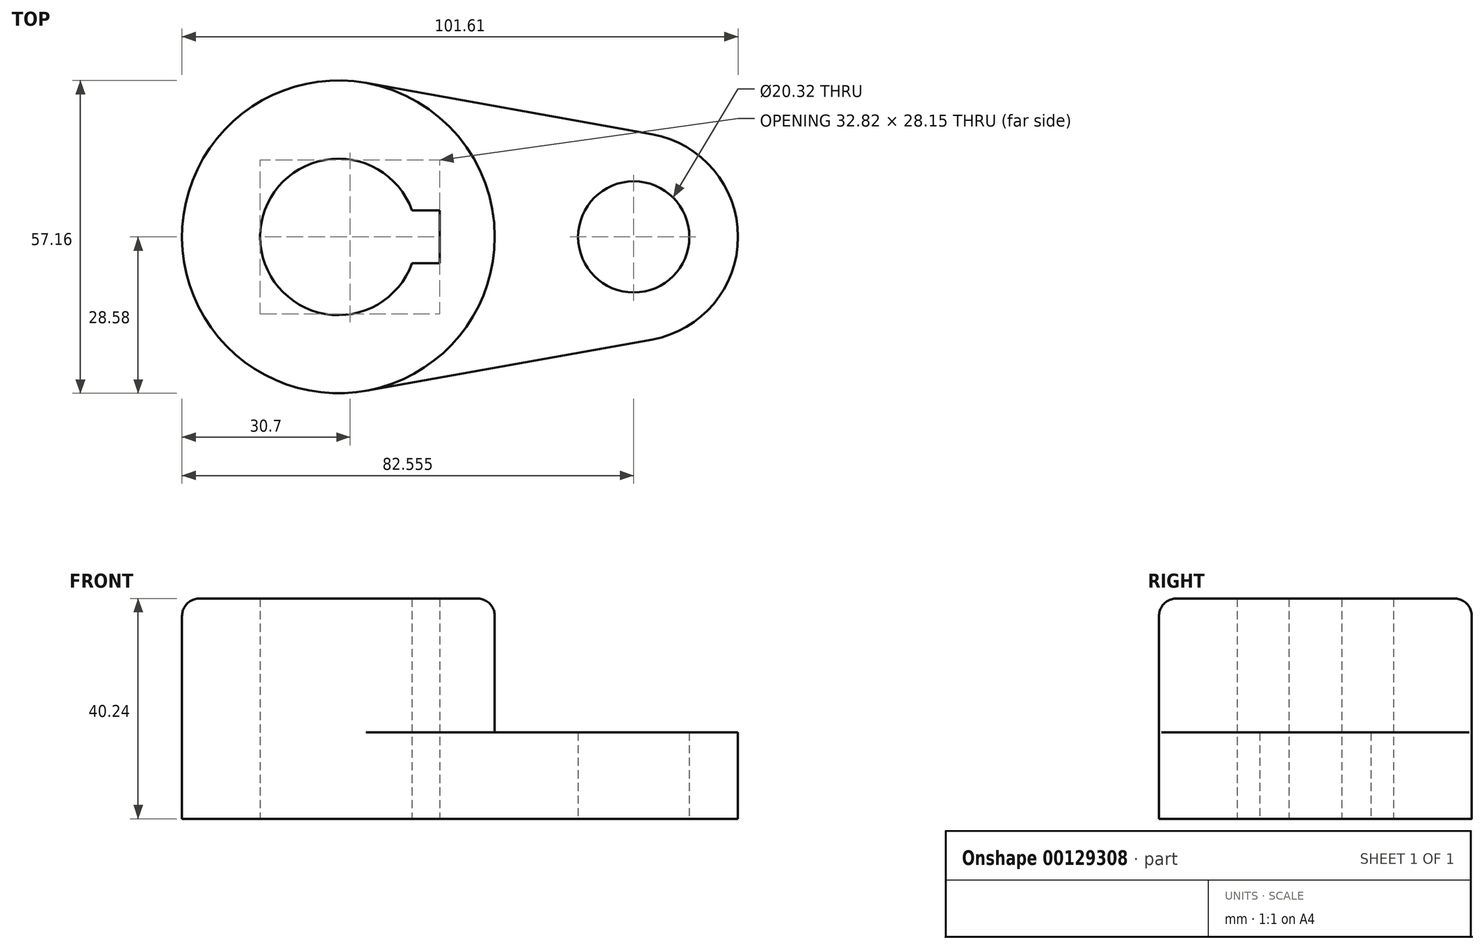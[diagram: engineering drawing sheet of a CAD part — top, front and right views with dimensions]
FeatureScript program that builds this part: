
annotation { "Feature Type Name" : "Feature", "Feature Type Description" : "" }
export const myFeature = defineFeature(function(context is Context, id is Id, definition is map)
    precondition{}
    {
        {
            var Q0;
            Q0=qCreatedBy(makeId("Top.planeOp"),FACE);
            var sketch = newSketch(context, id + "F0", { "sketchPlane" : qUnion([Q0])});
            skCircle(sketch, "E0", {"center": v(0, 0) * mm, "radius": 28.58 * mm});
            skCircle(sketch, "E1", {"center": v(53.98, 0) * mm, "radius": 19.05 * mm});
            skCircle(sketch, "E2", {"center": v(0, 0) * mm, "radius": 14.29 * mm});
            skLineSegment(sketch, "E3", {"start": v(5.04, 28.13) * mm, "end": v(57.34, 18.75) * mm});
            skLineSegment(sketch, "E4", {"start": v(5.04, -28.13) * mm, "end": v(57.34, -18.75) * mm});
            skCircle(sketch, "E5", {"center": v(53.98, 0) * mm, "radius": 10.16 * mm});
            skLineSegment(sketch, "E6.rect.bottom", {"start": v(18.53, 4.83) * mm, "end": v(-18.53, 4.83) * mm});
            skLineSegment(sketch, "E6.rect.top", {"start": v(18.53, -4.83) * mm, "end": v(-18.53, -4.83) * mm});
            skLineSegment(sketch, "E6.rect.left", {"start": v(18.53, 4.83) * mm, "end": v(18.53, -4.83) * mm});
            skLineSegment(sketch, "E6.rect.right", {"start": v(-18.53, 4.83) * mm, "end": v(-18.53, -4.83) * mm});
            skPoint(sketch, "E7", {"position": v(13.45, -4.83) * mm});
            skSolve(sketch);
        }
        {
            var Q0;
            {var subQ1=sQuery(id+"F0.wireOp",EDGE,"5164668d-e62a-4045-9f85-0bc2aa6b745a");Q0=makeQuery(id+"F0.imprint","IMPRINT",FACE,{"disambiguationData":[TD([[makeQuery(id+"F0.imprint","IMPRINT",EDGE,{"derivedFrom":subQ1}),1.0]])]});}
            var Q1;
            {var subQ0=sQuery(id+"F0.wireOp",EDGE,"E6.rect.left");Q1=makeQuery(id+"F0.imprint","IMPRINT",FACE,{"disambiguationData":[TD([[makeQuery(id+"F0.imprint","IMPRINT",EDGE,{"derivedFrom":subQ0}),1.0]])]});}
            var Q2;
            {var subQ1=sQuery(id+"F0.wireOp",EDGE,"E3");Q2=makeQuery(id+"F0.imprint","IMPRINT",FACE,{"disambiguationData":[TD([[makeQuery(id+"F0.imprint","IMPRINT",EDGE,{"derivedFrom":subQ1}),-1.0]])]});}
            var Q3;
            {var subQ0=sQuery(id+"F0.wireOp",EDGE,"E6.rect.right");Q3=makeQuery(id+"F0.imprint","IMPRINT",FACE,{"disambiguationData":[TD([[makeQuery(id+"F0.imprint","IMPRINT",EDGE,{"derivedFrom":subQ0}),1.0]])]});}
            var Q4;
            Q4=makeQuery(id+"F0.imprint","IMPRINT",FACE,{"disambiguationData":[TD([[makeQuery(id+"F0.imprint","IMPRINT",EDGE,{"derivedFrom":sQuery(id+"F0.wireOp",EDGE,"E5")}),-1.0]])]});
            extrude(context, id + "F1", {"entities" : qUnion([Q0, Q1, Q2, Q3, Q4]), "depth" : 15.76 * mm});
        }
        {
            var Q0;
            {var subQ0=sQuery(id+"F0.wireOp",EDGE,"E6.rect.left");Q0=makeQuery(id+"F0.imprint","IMPRINT",FACE,{"disambiguationData":[TD([[makeQuery(id+"F0.imprint","IMPRINT",EDGE,{"derivedFrom":subQ0}),1.0]])]});}
            var Q1;
            {var subQ0=sQuery(id+"F0.wireOp",EDGE,"E6.rect.right");Q1=makeQuery(id+"F0.imprint","IMPRINT",FACE,{"disambiguationData":[TD([[makeQuery(id+"F0.imprint","IMPRINT",EDGE,{"derivedFrom":subQ0}),1.0]])]});}
            extrude(context, id + "F2", {"entities" : qUnion([Q0, Q1]), "operationType" : NewBodyOperationType.ADD, "depth" : 40.24 * mm});
        }
        {
            var Q0;
            Q0=makeQuery(id+"F2.opExtrude","CAP_EDGE",EDGE,{"disambiguationData":[OSD([sQuery(id+"F0.wireOp",EDGE,"E0")])],"isStart":false});
            fillet(context, id + "F3", {"entities" : qUnion([Q0]), "radius" : 3.17 * mm, "tangentPropagation" : true, "allowEdgeOverflow" : false});
        }
    });
